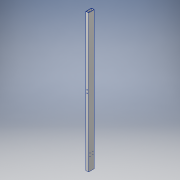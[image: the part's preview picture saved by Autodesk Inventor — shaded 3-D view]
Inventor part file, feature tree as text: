
AUTODESK INVENTOR PART (.ipt)
format: ipt  version: 2017 (Build 210142000, 142)  size: 145,920 bytes
history: native  units: in
note: dims shown in document units (in); Inventor stores cm internally (conversion verified against a paired STEP export)
features: sketch x5, extrude x3, hole x2
ambient origin geometry x8: Origin, YZ Plane, XZ Plane, XY Plane, X Axis, Y Axis, Z Axis, Center Point
bodies: Solid1 (feature_tree)
feature tree (10):
  extrude  "Extrusion1"  Depth=2.0in
  extrude  "Extrusion2"  Depth=1.75in
  extrude  "Extrusion3"  Depth=0.125in
  hole  "Hole1"  [1 undecoded]
  hole  "Hole3"  [1 undecoded]
  sketch  "Sketch2"  dims[d2=1.0in d3=2.0in]
  sketch  "Sketch3"  dims[d4=0.75in d5=1.75in]
  sketch  "Sketch4"  dims[d6=0.125in d7=0.125in]
  sketch  "Sketch5"  dims[d8=48.0in d9=0.0in d10=48.0in]
  sketch  "Sketch7"  dims[d11=24.0in d12=0.5in d13=0.25in d14=48.0in d15=0.0in d16=1.125in d17=1.125in d18=0.25in d19=0.0in d20=4.5in d21=0.5in d22=0.125in d24=0.125in d25=0.75in d26=0.375in d27=0.25in d28=0.5635in d29=0.125in d30=0.8108in d41=1.125in d42=0.75in d43=0.375in d44=0.25in d45=0.5635in d46=0.125in d47=0.8108in]
note: 2 required parameter values undecoded (feature->parameter linkage not recoverable at this tier; creation-order binding heuristic only, values carry confidence <= 0.55)
